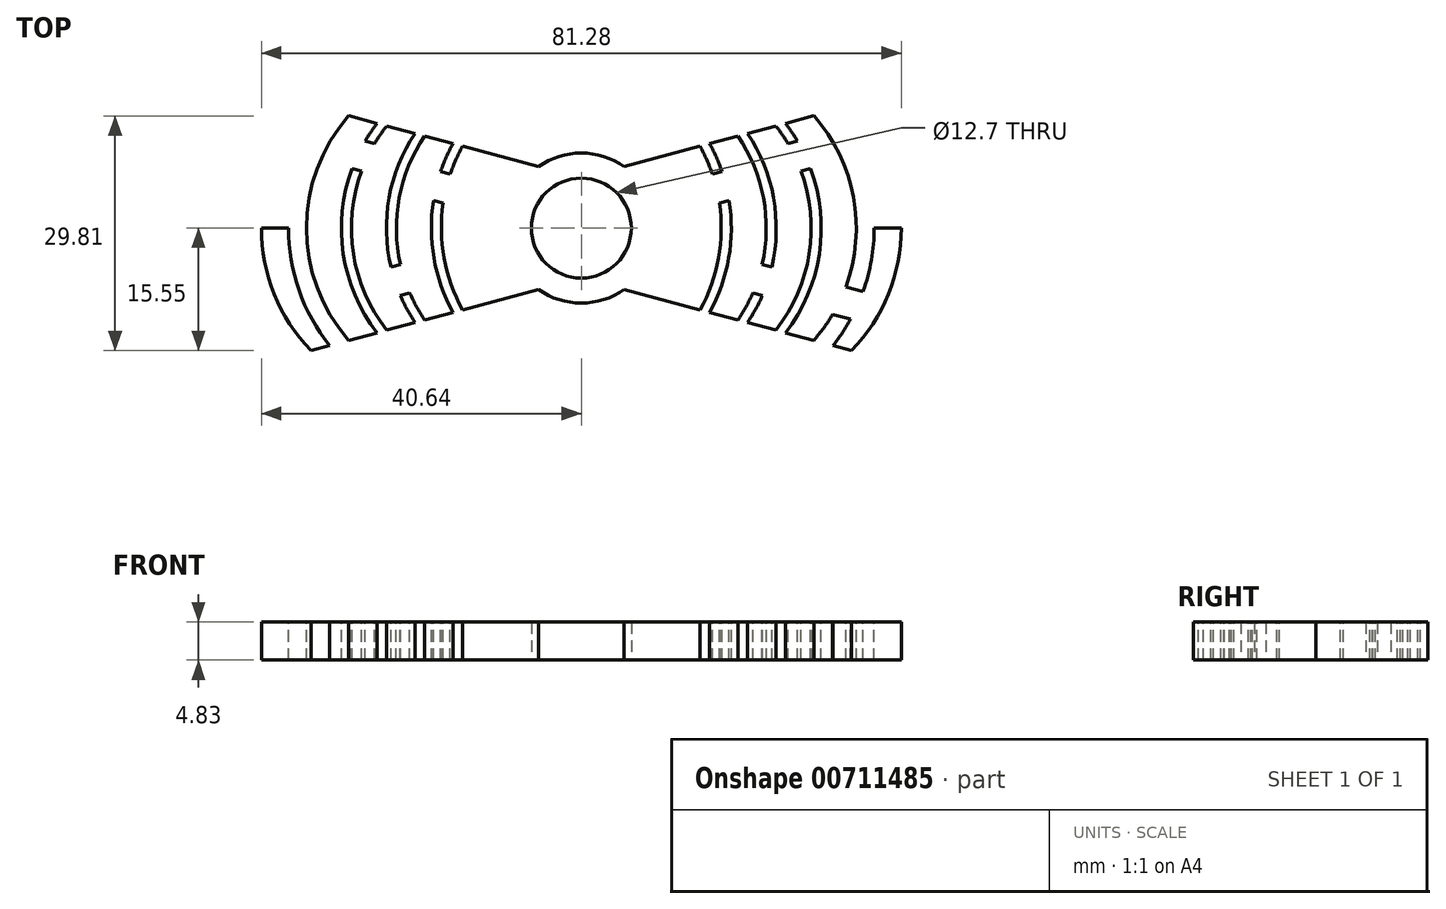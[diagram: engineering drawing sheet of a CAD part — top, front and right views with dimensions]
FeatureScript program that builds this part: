
annotation { "Feature Type Name" : "Feature", "Feature Type Description" : "" }
export const myFeature = defineFeature(function(context is Context, id is Id, definition is map)
    precondition{}
    {
        {
            var Q0;
            Q0=qCreatedBy(makeId("Top.planeOp"),FACE);
            var sketch = newSketch(context, id + "F0", { "sketchPlane" : qUnion([Q0])});
            skCircle(sketch, "E0", {"center": v(0, 0) * mm, "radius": 6.35 * mm});
            skCircle(sketch, "E1", {"center": v(0, 0) * mm, "radius": 9.53 * mm});
            skLineSegment(sketch, "E2", {"start": v(0, 0) * mm, "end": v(40.64, 0) * mm});
            skLineSegment(sketch, "E3", {"start": v(0, 0) * mm, "end": v(-40.64, 0) * mm});
            skLineSegment(sketch, "E4", {"start": v(0, 6.35) * mm, "end": v(34.35, 15.55) * mm});
            skLineSegment(sketch, "E5", {"start": v(0, -6.35) * mm, "end": v(34.35, -15.55) * mm});
            skLineSegment(sketch, "E6", {"start": v(0, -6.35) * mm, "end": v(-34.35, -15.55) * mm});
            skLineSegment(sketch, "E7", {"start": v(0, 6.35) * mm, "end": v(-34.35, 15.55) * mm});
            skArc(sketch, "E8", {"start": v(34.35, -15.55) * mm, "mid": v(40.64, 0) * mm, "end": v(34.35, 15.55) * mm});
            skArc(sketch, "E9", {"start": v(-34.35, 15.55) * mm, "mid": v(-40.64, 0) * mm, "end": v(-34.35, -15.55) * mm});
            skSolve(sketch);
        }
        {
            var Q0;
            Q0 = qSketchRegion(id + "F0", true);
            extrude(context, id + "F1", {"entities" : qUnion([Q0]), "depth" : 4.83 * mm, "offsetDistance" : 25.4 * mm});
        }
        {
            var Q0;
            Q0=makeQuery(id+"F1.opExtrude","CAP_FACE",FACE,{"disambiguationData":[OSD([sQuery(id+"F0.wireOp",EDGE,"E0"),sQuery(id+"F0.wireOp",EDGE,"E1"),sQuery(id+"F0.wireOp",EDGE,"E4"),sQuery(id+"F0.wireOp",EDGE,"E5"),sQuery(id+"F0.wireOp",EDGE,"E6"),sQuery(id+"F0.wireOp",EDGE,"E7"),sQuery(id+"F0.wireOp",EDGE,"E8"),sQuery(id+"F0.wireOp",EDGE,"E9")])],"isStart":false});
            var sketch = newSketch(context, id + "F2", { "sketchPlane" : qUnion([Q0])});
            skLineSegment(sketch, "E10", {"start": v(-6.35, 0) * mm, "end": v(-40.64, 0) * mm});
            skLineSegment(sketch, "E11", {"start": v(-5.45, -7.81) * mm, "end": v(-34.35, -15.55) * mm});
            skLineSegment(sketch, "E12", {"start": v(-34.35, 15.55) * mm, "end": v(-5.45, 7.81) * mm});
            skArc(sketch, "E13", {"start": v(-34.35, 15.55) * mm, "mid": v(-40.64, 0) * mm, "end": v(-34.35, -15.55) * mm});
            skLineSegment(sketch, "E14", {"start": v(5.45, -7.81) * mm, "end": v(34.35, -15.55) * mm});
            skLineSegment(sketch, "E15", {"start": v(6.35, 0) * mm, "end": v(40.64, 0) * mm});
            skLineSegment(sketch, "E16", {"start": v(5.45, 7.81) * mm, "end": v(34.35, 15.55) * mm});
            skLineSegment(sketch, "E17", {"start": v(-34.93, 0) * mm, "end": v(-34.93, 2.66) * mm});
            skLineSegment(sketch, "E18", {"start": v(-29.21, 0) * mm, "end": v(-29.21, 2.66) * mm});
            skLineSegment(sketch, "E19", {"start": v(-23.5, 0) * mm, "end": v(-23.5, 2.66) * mm});
            skLineSegment(sketch, "E20", {"start": v(-17.78, 0) * mm, "end": v(-17.78, 2.49) * mm});
            skLineSegment(sketch, "E21", {"start": v(-19.9, 11.68) * mm, "end": v(-20.56, 9.23) * mm});
            skLineSegment(sketch, "E22", {"start": v(-24.72, 12.97) * mm, "end": v(-25.37, 10.52) * mm});
            skLineSegment(sketch, "E23", {"start": v(-29.53, 14.26) * mm, "end": v(-30.19, 11.8) * mm});
            skLineSegment(sketch, "E24", {"start": v(-15.08, 10.4) * mm, "end": v(-15.74, 7.94) * mm});
            skLineSegment(sketch, "E25.MirrorCS", {"start": v(-29.53, -14.26) * mm, "end": v(-30.19, -11.8) * mm});
            skLineSegment(sketch, "E26.MirrorCS", {"start": v(-24.72, -12.97) * mm, "end": v(-25.37, -10.52) * mm});
            skLineSegment(sketch, "E27.MirrorCS", {"start": v(-19.9, -11.68) * mm, "end": v(-20.56, -9.23) * mm});
            skLineSegment(sketch, "E28.MirrorCS", {"start": v(-15.08, -10.4) * mm, "end": v(-15.74, -7.94) * mm});
            skArc(sketch, "E29", {"start": v(-29.53, 14.26) * mm, "mid": v(-34.93, 0) * mm, "end": v(-29.53, -14.26) * mm});
            skArc(sketch, "E30", {"start": v(-24.72, 12.97) * mm, "mid": v(-29.21, 0) * mm, "end": v(-24.72, -12.97) * mm});
            skArc(sketch, "E31", {"start": v(-19.9, 11.68) * mm, "mid": v(-23.5, 0) * mm, "end": v(-19.9, -11.68) * mm});
            skArc(sketch, "E32", {"start": v(-15.08, 10.4) * mm, "mid": v(-17.78, 0) * mm, "end": v(-15.08, -10.4) * mm});
            skArc(sketch, "E33", {"start": v(-31.99, 14.92) * mm, "mid": v(-37.2, 0) * mm, "end": v(-31.99, -14.92) * mm});
            skArc(sketch, "E34", {"start": v(-25.94, 13.3) * mm, "mid": v(-30.48, 0) * mm, "end": v(-25.94, -13.3) * mm});
            skArc(sketch, "E35", {"start": v(-21.13, 12.01) * mm, "mid": v(-24.76, 0) * mm, "end": v(-21.13, -12.01) * mm});
            skArc(sketch, "E36", {"start": v(-16.31, 10.72) * mm, "mid": v(-19.05, 0) * mm, "end": v(-16.31, -10.72) * mm});
            skLineSegment(sketch, "E37", {"start": v(-34.22, -11.57) * mm, "end": v(-31.93, -10.96) * mm});
            skLineSegment(sketch, "E38", {"start": v(-35.8, -8.05) * mm, "end": v(-33.6, -7.46) * mm});
            skLineSegment(sketch, "E39", {"start": v(-21.79, -8.24) * mm, "end": v(-23, -8.57) * mm});
            skLineSegment(sketch, "E40", {"start": v(-22.98, -4.62) * mm, "end": v(-24.2, -4.94) * mm});
            skLineSegment(sketch, "E41", {"start": v(-27.45, 11.08) * mm, "end": v(-26.24, 10.75) * mm});
            skLineSegment(sketch, "E42", {"start": v(-29.12, 7.58) * mm, "end": v(-27.91, 7.26) * mm});
            skLineSegment(sketch, "E43", {"start": v(-17.86, 7.2) * mm, "end": v(-16.65, 6.87) * mm});
            skLineSegment(sketch, "E44", {"start": v(-17.54, 3.16) * mm, "end": v(-18.78, 3.5) * mm});
            skLineSegment(sketch, "E45.MirrorCS", {"start": v(34.35, 15.55) * mm, "end": v(5.45, 7.81) * mm});
            skArc(sketch, "E46.MirrorCS", {"start": v(-21.13, 12.01) * mm, "mid": v(-24.77, 0) * mm, "end": v(-21.13, -12.01) * mm});
            skLineSegment(sketch, "E47.MirrorCS", {"start": v(-5.45, 7.81) * mm, "end": v(-34.35, 15.55) * mm});
            skArc(sketch, "E48.MirrorCS", {"start": v(-34.35, -15.55) * mm, "mid": v(-40.64, 0) * mm, "end": v(-34.35, 15.55) * mm});
            skLineSegment(sketch, "E49.MirrorCS", {"start": v(15.08, 10.4) * mm, "end": v(15.74, 7.94) * mm});
            skLineSegment(sketch, "E50.MirrorCS", {"start": v(15.08, -10.4) * mm, "end": v(15.74, -7.94) * mm});
            skLineSegment(sketch, "E51.MirrorCS", {"start": v(29.21, 0) * mm, "end": v(29.21, 2.66) * mm});
            skLineSegment(sketch, "E52.MirrorCS", {"start": v(24.72, -12.97) * mm, "end": v(25.37, -10.52) * mm});
            skLineSegment(sketch, "E53.MirrorCS", {"start": v(19.9, 11.68) * mm, "end": v(20.56, 9.23) * mm});
            skLineSegment(sketch, "E54.MirrorCS", {"start": v(34.93, 0) * mm, "end": v(34.93, 2.66) * mm});
            skLineSegment(sketch, "E55.MirrorCS", {"start": v(23.5, 0) * mm, "end": v(23.5, 2.66) * mm});
            skLineSegment(sketch, "E56.MirrorCS", {"start": v(19.9, -11.68) * mm, "end": v(20.56, -9.23) * mm});
            skLineSegment(sketch, "E57.MirrorCS", {"start": v(17.78, 0) * mm, "end": v(17.78, 2.49) * mm});
            skLineSegment(sketch, "E58.MirrorCS", {"start": v(24.72, 12.97) * mm, "end": v(25.37, 10.52) * mm});
            skLineSegment(sketch, "E59.MirrorCS", {"start": v(29.53, 14.26) * mm, "end": v(30.19, 11.8) * mm});
            skLineSegment(sketch, "E60.MirrorCS", {"start": v(29.53, -14.26) * mm, "end": v(30.19, -11.8) * mm});
            skLineSegment(sketch, "E61.MirrorCS", {"start": v(17.54, 3.16) * mm, "end": v(18.78, 3.5) * mm});
            skLineSegment(sketch, "E62.MirrorCS", {"start": v(17.86, 7.2) * mm, "end": v(16.65, 6.87) * mm});
            skLineSegment(sketch, "E63.MirrorCS", {"start": v(22.98, -4.62) * mm, "end": v(24.2, -4.94) * mm});
            skLineSegment(sketch, "E64.MirrorCS", {"start": v(21.79, -8.24) * mm, "end": v(23, -8.57) * mm});
            skLineSegment(sketch, "E65.MirrorCS", {"start": v(29.12, 7.58) * mm, "end": v(27.91, 7.26) * mm});
            skLineSegment(sketch, "E66.MirrorCS", {"start": v(34.22, -11.57) * mm, "end": v(31.93, -10.96) * mm});
            skLineSegment(sketch, "E67.MirrorCS", {"start": v(35.8, -8.05) * mm, "end": v(33.6, -7.46) * mm});
            skLineSegment(sketch, "E68.MirrorCS", {"start": v(27.45, 11.08) * mm, "end": v(26.24, 10.75) * mm});
            skArc(sketch, "E69.MirrorCS", {"start": v(24.72, 12.97) * mm, "mid": v(29.21, 0) * mm, "end": v(24.72, -12.97) * mm});
            skArc(sketch, "E70.MirrorCS", {"start": v(19.9, 11.68) * mm, "mid": v(23.5, 0) * mm, "end": v(19.9, -11.68) * mm});
            skArc(sketch, "E71.MirrorCS", {"start": v(15.08, 10.4) * mm, "mid": v(17.78, 0) * mm, "end": v(15.08, -10.4) * mm});
            skArc(sketch, "E72.MirrorCS", {"start": v(29.53, 14.26) * mm, "mid": v(34.93, 0) * mm, "end": v(29.53, -14.26) * mm});
            skArc(sketch, "E73.MirrorCS", {"start": v(25.94, 13.3) * mm, "mid": v(30.48, 0) * mm, "end": v(25.94, -13.3) * mm});
            skArc(sketch, "E74.MirrorCS", {"start": v(21.13, 12.01) * mm, "mid": v(24.76, 0) * mm, "end": v(21.13, -12.01) * mm});
            skArc(sketch, "E75.MirrorCS", {"start": v(31.99, 14.92) * mm, "mid": v(37.2, 0) * mm, "end": v(31.99, -14.92) * mm});
            skArc(sketch, "E76.MirrorCS", {"start": v(16.31, 10.72) * mm, "mid": v(19.05, 0) * mm, "end": v(16.31, -10.72) * mm});
            skArc(sketch, "E77.MirrorCS", {"start": v(34.35, 15.55) * mm, "mid": v(40.64, 0) * mm, "end": v(34.35, -15.55) * mm});
            skArc(sketch, "E78.MirrorCS", {"start": v(21.13, 12.01) * mm, "mid": v(24.77, 0) * mm, "end": v(21.13, -12.01) * mm});
            skArc(sketch, "E79.MirrorCS", {"start": v(34.35, -15.55) * mm, "mid": v(40.64, 0) * mm, "end": v(34.35, 15.55) * mm});
            skSolve(sketch);
        }
        {
            var Q0;
            {var subQ0=sQuery(id+"F2.wireOp",EDGE,"E38");Q0=makeQuery(id+"F2.imprint","IMPRINT",FACE,{"disambiguationData":[TD([[makeQuery(id+"F2.imprint","IMPRINT",EDGE,{"derivedFrom":subQ0}),1.0]])]});}
            var Q1;
            {var subQ0=sQuery(id+"F2.wireOp",EDGE,"E47.MirrorCS");var subQ1=sQuery(id+"F2.wireOp",EDGE,"E33");var subQ2=makeQuery(id+"F2.imprint","INTERSECT",VERTEX,{"derivedFrom":[subQ1,subQ0]});Q1=makeQuery(id+"F2.imprint","IMPRINT",FACE,{"disambiguationData":[TD([[makeQuery(id+"F2.imprint","IMPRINT",EDGE,{"disambiguationData":[TD([[subQ2,-1.0]])],"derivedFrom":subQ1}),1.0]])]});}
            var Q2;
            {var subQ0=sQuery(id+"F2.wireOp",EDGE,"E37");Q2=makeQuery(id+"F2.imprint","IMPRINT",FACE,{"disambiguationData":[TD([[makeQuery(id+"F2.imprint","IMPRINT",EDGE,{"derivedFrom":subQ0}),-1.0]])]});}
            var Q3;
            {var subQ0=sQuery(id+"F2.wireOp",EDGE,"E30");var subQ1=sQuery(id+"F2.wireOp",EDGE,"E10");var subQ2=makeQuery(id+"F2.imprint","INTERSECT",VERTEX,{"derivedFrom":[subQ1,subQ0]});Q3=makeQuery(id+"F2.imprint","IMPRINT",FACE,{"disambiguationData":[TD([[makeQuery(id+"F2.imprint","IMPRINT",EDGE,{"disambiguationData":[TD([[subQ2,-1.0]])],"derivedFrom":subQ1}),1.0]])]});}
            var Q4;
            {var subQ0=sQuery(id+"F2.wireOp",EDGE,"E41");Q4=makeQuery(id+"F2.imprint","IMPRINT",FACE,{"disambiguationData":[TD([[makeQuery(id+"F2.imprint","IMPRINT",EDGE,{"derivedFrom":subQ0}),1.0]])]});}
            var Q5;
            {var subQ0=sQuery(id+"F2.wireOp",EDGE,"E42");Q5=makeQuery(id+"F2.imprint","IMPRINT",FACE,{"disambiguationData":[TD([[makeQuery(id+"F2.imprint","IMPRINT",EDGE,{"derivedFrom":subQ0}),-1.0]])]});}
            var Q6;
            {var subQ0=sQuery(id+"F2.wireOp",EDGE,"E31");var subQ1=sQuery(id+"F2.wireOp",EDGE,"E10");var subQ2=makeQuery(id+"F2.imprint","INTERSECT",VERTEX,{"derivedFrom":[subQ1,subQ0]});Q6=makeQuery(id+"F2.imprint","IMPRINT",FACE,{"disambiguationData":[TD([[makeQuery(id+"F2.imprint","IMPRINT",EDGE,{"disambiguationData":[TD([[subQ2,-1.0]])],"derivedFrom":subQ1}),-1.0]])]});}
            var Q7;
            {var subQ0=sQuery(id+"F2.wireOp",EDGE,"E40");Q7=makeQuery(id+"F2.imprint","IMPRINT",FACE,{"disambiguationData":[TD([[makeQuery(id+"F2.imprint","IMPRINT",EDGE,{"derivedFrom":subQ0}),-1.0]])]});}
            var Q8;
            {var subQ0=sQuery(id+"F2.wireOp",EDGE,"E39");Q8=makeQuery(id+"F2.imprint","IMPRINT",FACE,{"disambiguationData":[TD([[makeQuery(id+"F2.imprint","IMPRINT",EDGE,{"derivedFrom":subQ0}),1.0]])]});}
            var Q9;
            {var subQ0=sQuery(id+"F2.wireOp",EDGE,"E32");var subQ1=sQuery(id+"F2.wireOp",EDGE,"E10");var subQ2=makeQuery(id+"F2.imprint","INTERSECT",VERTEX,{"derivedFrom":[subQ1,subQ0]});Q9=makeQuery(id+"F2.imprint","IMPRINT",FACE,{"disambiguationData":[TD([[makeQuery(id+"F2.imprint","IMPRINT",EDGE,{"disambiguationData":[TD([[subQ2,-1.0]])],"derivedFrom":subQ1}),1.0]])]});}
            var Q10;
            {var subQ0=sQuery(id+"F2.wireOp",EDGE,"E44");Q10=makeQuery(id+"F2.imprint","IMPRINT",FACE,{"disambiguationData":[TD([[makeQuery(id+"F2.imprint","IMPRINT",EDGE,{"derivedFrom":subQ0}),1.0]])]});}
            var Q11;
            {var subQ0=sQuery(id+"F2.wireOp",EDGE,"E43");Q11=makeQuery(id+"F2.imprint","IMPRINT",FACE,{"disambiguationData":[TD([[makeQuery(id+"F2.imprint","IMPRINT",EDGE,{"derivedFrom":subQ0}),1.0]])]});}
            var Q12;
            {var subQ0=sQuery(id+"F2.wireOp",EDGE,"E71.MirrorCS");var subQ1=sQuery(id+"F2.wireOp",EDGE,"E15");var subQ2=makeQuery(id+"F2.imprint","INTERSECT",VERTEX,{"derivedFrom":[subQ1,subQ0]});Q12=makeQuery(id+"F2.imprint","IMPRINT",FACE,{"disambiguationData":[TD([[makeQuery(id+"F2.imprint","IMPRINT",EDGE,{"disambiguationData":[TD([[subQ2,-1.0]])],"derivedFrom":subQ1}),-1.0]])]});}
            var Q13;
            {var subQ5=sQuery(id+"F2.wireOp",EDGE,"E61.MirrorCS");Q13=makeQuery(id+"F2.imprint","IMPRINT",FACE,{"disambiguationData":[TD([[makeQuery(id+"F2.imprint","IMPRINT",EDGE,{"derivedFrom":subQ5}),-1.0]])]});}
            var Q14;
            {var subQ5=sQuery(id+"F2.wireOp",EDGE,"E62.MirrorCS");Q14=makeQuery(id+"F2.imprint","IMPRINT",FACE,{"disambiguationData":[TD([[makeQuery(id+"F2.imprint","IMPRINT",EDGE,{"derivedFrom":subQ5}),-1.0]])]});}
            var Q15;
            {var subQ0=sQuery(id+"F2.wireOp",EDGE,"E70.MirrorCS");var subQ1=sQuery(id+"F2.wireOp",EDGE,"E15");var subQ2=makeQuery(id+"F2.imprint","INTERSECT",VERTEX,{"derivedFrom":[subQ1,subQ0]});Q15=makeQuery(id+"F2.imprint","IMPRINT",FACE,{"disambiguationData":[TD([[makeQuery(id+"F2.imprint","IMPRINT",EDGE,{"disambiguationData":[TD([[subQ2,-1.0]])],"derivedFrom":subQ1}),1.0]])]});}
            var Q16;
            {var subQ5=sQuery(id+"F2.wireOp",EDGE,"E63.MirrorCS");Q16=makeQuery(id+"F2.imprint","IMPRINT",FACE,{"disambiguationData":[TD([[makeQuery(id+"F2.imprint","IMPRINT",EDGE,{"derivedFrom":subQ5}),1.0]])]});}
            var Q17;
            {var subQ5=sQuery(id+"F2.wireOp",EDGE,"E64.MirrorCS");Q17=makeQuery(id+"F2.imprint","IMPRINT",FACE,{"disambiguationData":[TD([[makeQuery(id+"F2.imprint","IMPRINT",EDGE,{"derivedFrom":subQ5}),-1.0]])]});}
            var Q18;
            {var subQ0=sQuery(id+"F2.wireOp",EDGE,"E69.MirrorCS");var subQ1=sQuery(id+"F2.wireOp",EDGE,"E15");var subQ2=makeQuery(id+"F2.imprint","INTERSECT",VERTEX,{"derivedFrom":[subQ1,subQ0]});Q18=makeQuery(id+"F2.imprint","IMPRINT",FACE,{"disambiguationData":[TD([[makeQuery(id+"F2.imprint","IMPRINT",EDGE,{"disambiguationData":[TD([[subQ2,-1.0]])],"derivedFrom":subQ1}),-1.0]])]});}
            var Q19;
            {var subQ5=sQuery(id+"F2.wireOp",EDGE,"E65.MirrorCS");Q19=makeQuery(id+"F2.imprint","IMPRINT",FACE,{"disambiguationData":[TD([[makeQuery(id+"F2.imprint","IMPRINT",EDGE,{"derivedFrom":subQ5}),1.0]])]});}
            var Q20;
            {var subQ5=sQuery(id+"F2.wireOp",EDGE,"E68.MirrorCS");Q20=makeQuery(id+"F2.imprint","IMPRINT",FACE,{"disambiguationData":[TD([[makeQuery(id+"F2.imprint","IMPRINT",EDGE,{"derivedFrom":subQ5}),-1.0]])]});}
            var Q21;
            {var subQ0=sQuery(id+"F2.wireOp",EDGE,"E72.MirrorCS");var subQ1=sQuery(id+"F2.wireOp",EDGE,"E15");var subQ2=makeQuery(id+"F2.imprint","INTERSECT",VERTEX,{"derivedFrom":[subQ1,subQ0]});Q21=makeQuery(id+"F2.imprint","IMPRINT",FACE,{"disambiguationData":[TD([[makeQuery(id+"F2.imprint","IMPRINT",EDGE,{"disambiguationData":[TD([[subQ2,-1.0]])],"derivedFrom":subQ1}),1.0]])]});}
            var Q22;
            {var subQ5=sQuery(id+"F2.wireOp",EDGE,"E67.MirrorCS");Q22=makeQuery(id+"F2.imprint","IMPRINT",FACE,{"disambiguationData":[TD([[makeQuery(id+"F2.imprint","IMPRINT",EDGE,{"derivedFrom":subQ5}),-1.0]])]});}
            var Q23;
            {var subQ5=sQuery(id+"F2.wireOp",EDGE,"E66.MirrorCS");Q23=makeQuery(id+"F2.imprint","IMPRINT",FACE,{"disambiguationData":[TD([[makeQuery(id+"F2.imprint","IMPRINT",EDGE,{"derivedFrom":subQ5}),1.0]])]});}
            extrude(context, id + "F3", {"entities" : qUnion([Q0, Q1, Q2, Q3, Q4, Q5, Q6, Q7, Q8, Q9, Q10, Q11, Q12, Q13, Q14, Q15, Q16, Q17, Q18, Q19, Q20, Q21, Q22, Q23]), "operationType" : NewBodyOperationType.REMOVE, "oppositeDirection" : true, "depth" : 25.4 * mm, "offsetDistance" : 25.4 * mm});
        }
    });
